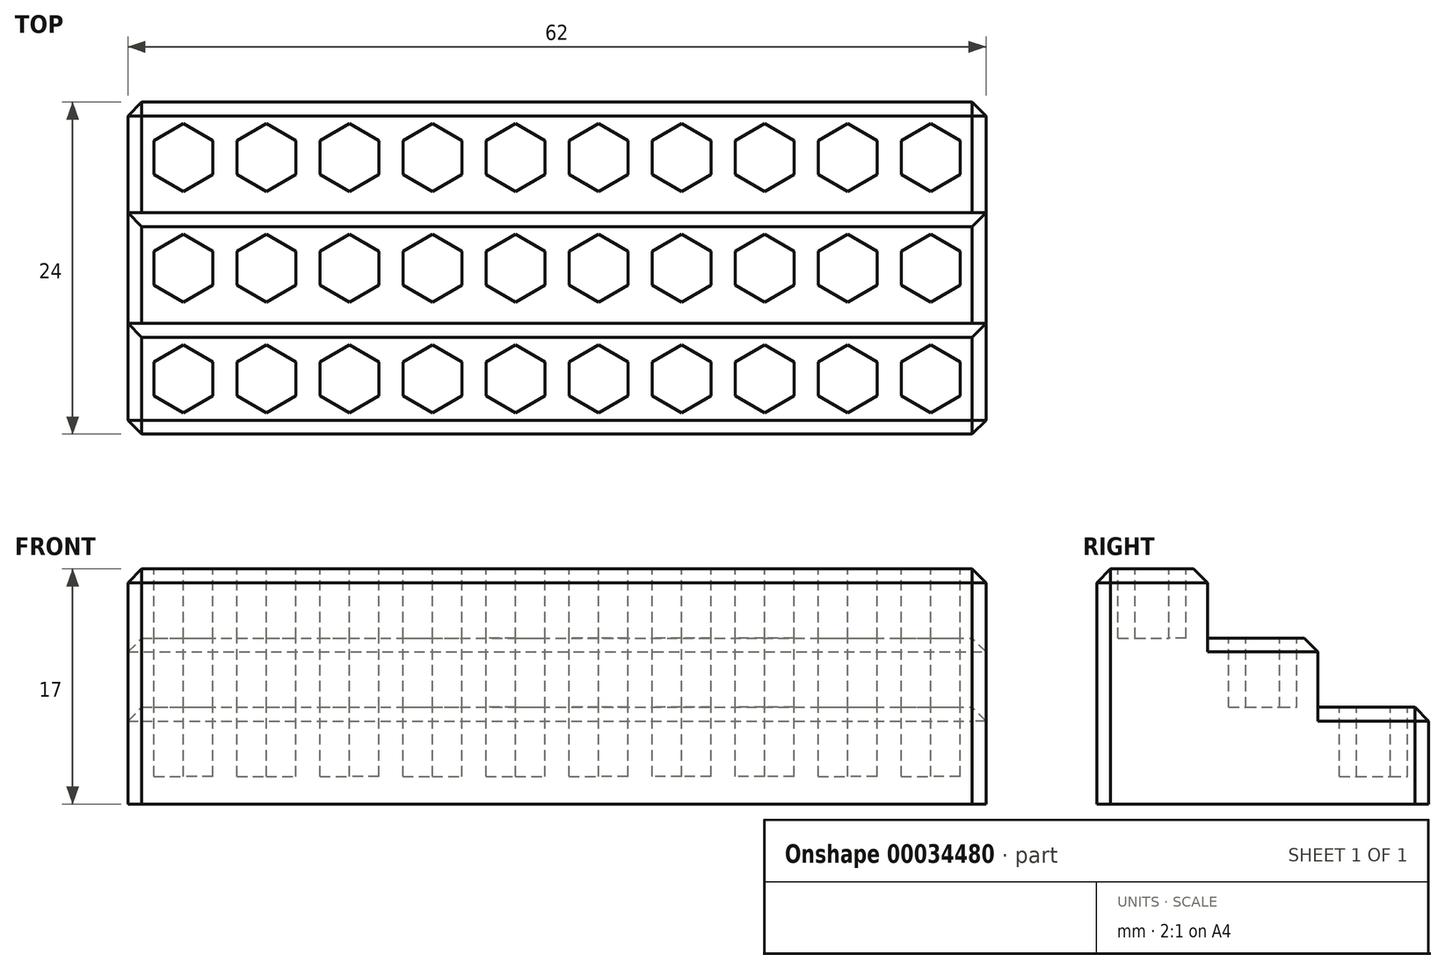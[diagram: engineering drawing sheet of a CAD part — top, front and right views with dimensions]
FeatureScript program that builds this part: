
annotation { "Feature Type Name" : "Feature", "Feature Type Description" : "" }
export const myFeature = defineFeature(function(context is Context, id is Id, definition is map)
    precondition{}
    {
        {
            var Q0;
            Q0=qCreatedBy(makeId("Top.planeOp"),FACE);
            var sketch = newSketch(context, id + "F0", { "sketchPlane" : qUnion([Q0])});
            skLineSegment(sketch, "E0.bottom", {"start": v(0, 0) * mm, "end": v(62, 0) * mm});
            skLineSegment(sketch, "E0.top", {"start": v(0, 8) * mm, "end": v(62, 8) * mm});
            skLineSegment(sketch, "E0.left", {"start": v(0, 0) * mm, "end": v(0, 8) * mm});
            skLineSegment(sketch, "E0.right", {"start": v(62, 0) * mm, "end": v(62, 8) * mm});
            skCircle(sketch, "E1.cCircle", {"center": v(4, 4) * mm, "radius": 2.13 * mm, "construction": true});
            skPoint(sketch, "E1.cCircle.centerSnap0", {"position": v(0, 4) * mm});
            skPoint(sketch, "E1.cCircle.perimeterSnap0", {"position": v(0, 4) * mm});
            skLineSegment(sketch, "E1.0", {"start": v(1.87, 2.77) * mm, "end": v(1.87, 5.23) * mm});
            skLineSegment(sketch, "E1.1", {"start": v(1.87, 5.23) * mm, "end": v(4, 6.45) * mm});
            skLineSegment(sketch, "E1.2", {"start": v(4, 6.45) * mm, "end": v(6.12, 5.23) * mm});
            skLineSegment(sketch, "E1.3", {"start": v(6.12, 5.23) * mm, "end": v(6.12, 2.77) * mm});
            skLineSegment(sketch, "E1.4", {"start": v(6.12, 2.77) * mm, "end": v(4, 1.55) * mm});
            skLineSegment(sketch, "E1.5", {"start": v(4, 1.55) * mm, "end": v(1.87, 2.77) * mm});
            skPoint(sketch, "E1.0.midPoint", {"position": v(1.87, 4) * mm});
            skPoint(sketch, "E1.0.midPoint.positionSnap0", {"position": v(0, 4) * mm});
            skCircle(sketch, "E2.1.0.0", {"center": v(10, 4) * mm, "radius": 2.13 * mm, "construction": true});
            skLineSegment(sketch, "E2.1.0.1", {"start": v(7.87, 5.23) * mm, "end": v(10, 6.45) * mm});
            skLineSegment(sketch, "E2.1.0.2", {"start": v(10, 6.45) * mm, "end": v(12.12, 5.23) * mm});
            skLineSegment(sketch, "E2.1.0.3", {"start": v(12.12, 5.23) * mm, "end": v(12.12, 2.77) * mm});
            skLineSegment(sketch, "E2.1.0.4", {"start": v(12.12, 2.77) * mm, "end": v(10, 1.55) * mm});
            skLineSegment(sketch, "E2.1.0.5", {"start": v(10, 1.55) * mm, "end": v(7.88, 2.77) * mm});
            skPoint(sketch, "E2.1.0.6", {"position": v(7.88, 4) * mm});
            skLineSegment(sketch, "E2.1.0.7", {"start": v(7.88, 2.77) * mm, "end": v(7.88, 5.23) * mm});
            skCircle(sketch, "E2.2.0.0", {"center": v(16, 4) * mm, "radius": 2.13 * mm, "construction": true});
            skLineSegment(sketch, "E2.2.0.1", {"start": v(13.87, 5.23) * mm, "end": v(16, 6.45) * mm});
            skLineSegment(sketch, "E2.2.0.2", {"start": v(16, 6.45) * mm, "end": v(18.13, 5.23) * mm});
            skLineSegment(sketch, "E2.2.0.3", {"start": v(18.12, 5.23) * mm, "end": v(18.12, 2.77) * mm});
            skLineSegment(sketch, "E2.2.0.4", {"start": v(18.13, 2.77) * mm, "end": v(16, 1.55) * mm});
            skLineSegment(sketch, "E2.2.0.5", {"start": v(16, 1.55) * mm, "end": v(13.87, 2.77) * mm});
            skPoint(sketch, "E2.2.0.6", {"position": v(13.87, 4) * mm});
            skLineSegment(sketch, "E2.2.0.7", {"start": v(13.87, 2.77) * mm, "end": v(13.87, 5.23) * mm});
            skCircle(sketch, "E2.3.0.0", {"center": v(22, 4) * mm, "radius": 2.13 * mm, "construction": true});
            skLineSegment(sketch, "E2.3.0.1", {"start": v(19.87, 5.23) * mm, "end": v(22, 6.45) * mm});
            skLineSegment(sketch, "E2.3.0.2", {"start": v(22, 6.45) * mm, "end": v(24.12, 5.23) * mm});
            skLineSegment(sketch, "E2.3.0.3", {"start": v(24.12, 5.23) * mm, "end": v(24.12, 2.77) * mm});
            skLineSegment(sketch, "E2.3.0.4", {"start": v(24.12, 2.77) * mm, "end": v(22, 1.55) * mm});
            skLineSegment(sketch, "E2.3.0.5", {"start": v(22, 1.55) * mm, "end": v(19.88, 2.77) * mm});
            skPoint(sketch, "E2.3.0.6", {"position": v(19.88, 4) * mm});
            skLineSegment(sketch, "E2.3.0.7", {"start": v(19.88, 2.77) * mm, "end": v(19.88, 5.23) * mm});
            skCircle(sketch, "E2.4.0.0", {"center": v(28, 4) * mm, "radius": 2.13 * mm, "construction": true});
            skLineSegment(sketch, "E2.4.0.1", {"start": v(25.87, 5.23) * mm, "end": v(28, 6.45) * mm});
            skLineSegment(sketch, "E2.4.0.2", {"start": v(28, 6.45) * mm, "end": v(30.12, 5.23) * mm});
            skLineSegment(sketch, "E2.4.0.3", {"start": v(30.12, 5.23) * mm, "end": v(30.12, 2.77) * mm});
            skLineSegment(sketch, "E2.4.0.4", {"start": v(30.12, 2.77) * mm, "end": v(28, 1.55) * mm});
            skLineSegment(sketch, "E2.4.0.5", {"start": v(28, 1.55) * mm, "end": v(25.88, 2.77) * mm});
            skPoint(sketch, "E2.4.0.6", {"position": v(25.88, 4) * mm});
            skLineSegment(sketch, "E2.4.0.7", {"start": v(25.88, 2.77) * mm, "end": v(25.88, 5.23) * mm});
            skCircle(sketch, "E2.5.0.0", {"center": v(34, 4) * mm, "radius": 2.13 * mm, "construction": true});
            skLineSegment(sketch, "E2.5.0.1", {"start": v(31.87, 5.23) * mm, "end": v(34, 6.45) * mm});
            skLineSegment(sketch, "E2.5.0.2", {"start": v(34, 6.45) * mm, "end": v(36.12, 5.23) * mm});
            skLineSegment(sketch, "E2.5.0.3", {"start": v(36.12, 5.23) * mm, "end": v(36.12, 2.77) * mm});
            skLineSegment(sketch, "E2.5.0.4", {"start": v(36.12, 2.77) * mm, "end": v(34, 1.55) * mm});
            skLineSegment(sketch, "E2.5.0.5", {"start": v(34, 1.55) * mm, "end": v(31.88, 2.77) * mm});
            skPoint(sketch, "E2.5.0.6", {"position": v(31.88, 4) * mm});
            skLineSegment(sketch, "E2.5.0.7", {"start": v(31.88, 2.77) * mm, "end": v(31.88, 5.23) * mm});
            skCircle(sketch, "E2.6.0.0", {"center": v(40, 4) * mm, "radius": 2.13 * mm, "construction": true});
            skLineSegment(sketch, "E2.6.0.1", {"start": v(37.87, 5.23) * mm, "end": v(40, 6.45) * mm});
            skLineSegment(sketch, "E2.6.0.2", {"start": v(40, 6.45) * mm, "end": v(42.12, 5.23) * mm});
            skLineSegment(sketch, "E2.6.0.3", {"start": v(42.12, 5.23) * mm, "end": v(42.12, 2.77) * mm});
            skLineSegment(sketch, "E2.6.0.4", {"start": v(42.12, 2.77) * mm, "end": v(40, 1.55) * mm});
            skLineSegment(sketch, "E2.6.0.5", {"start": v(40, 1.55) * mm, "end": v(37.88, 2.77) * mm});
            skPoint(sketch, "E2.6.0.6", {"position": v(37.88, 4) * mm});
            skLineSegment(sketch, "E2.6.0.7", {"start": v(37.88, 2.77) * mm, "end": v(37.88, 5.23) * mm});
            skCircle(sketch, "E2.7.0.0", {"center": v(46, 4) * mm, "radius": 2.13 * mm, "construction": true});
            skLineSegment(sketch, "E2.7.0.1", {"start": v(43.87, 5.23) * mm, "end": v(46, 6.45) * mm});
            skLineSegment(sketch, "E2.7.0.2", {"start": v(46, 6.45) * mm, "end": v(48.12, 5.23) * mm});
            skLineSegment(sketch, "E2.7.0.3", {"start": v(48.12, 5.23) * mm, "end": v(48.12, 2.77) * mm});
            skLineSegment(sketch, "E2.7.0.4", {"start": v(48.12, 2.77) * mm, "end": v(46, 1.55) * mm});
            skLineSegment(sketch, "E2.7.0.5", {"start": v(46, 1.55) * mm, "end": v(43.88, 2.77) * mm});
            skPoint(sketch, "E2.7.0.6", {"position": v(43.88, 4) * mm});
            skLineSegment(sketch, "E2.7.0.7", {"start": v(43.88, 2.77) * mm, "end": v(43.88, 5.23) * mm});
            skCircle(sketch, "E2.8.0.0", {"center": v(52, 4) * mm, "radius": 2.13 * mm, "construction": true});
            skLineSegment(sketch, "E2.8.0.1", {"start": v(49.87, 5.23) * mm, "end": v(52, 6.45) * mm});
            skLineSegment(sketch, "E2.8.0.2", {"start": v(52, 6.45) * mm, "end": v(54.12, 5.23) * mm});
            skLineSegment(sketch, "E2.8.0.3", {"start": v(54.12, 5.23) * mm, "end": v(54.12, 2.77) * mm});
            skLineSegment(sketch, "E2.8.0.4", {"start": v(54.12, 2.77) * mm, "end": v(52, 1.55) * mm});
            skLineSegment(sketch, "E2.8.0.5", {"start": v(52, 1.55) * mm, "end": v(49.88, 2.77) * mm});
            skPoint(sketch, "E2.8.0.6", {"position": v(49.88, 4) * mm});
            skLineSegment(sketch, "E2.8.0.7", {"start": v(49.88, 2.77) * mm, "end": v(49.88, 5.23) * mm});
            skCircle(sketch, "E2.9.0.0", {"center": v(58, 4) * mm, "radius": 2.13 * mm, "construction": true});
            skLineSegment(sketch, "E2.9.0.1", {"start": v(55.87, 5.23) * mm, "end": v(58, 6.45) * mm});
            skLineSegment(sketch, "E2.9.0.2", {"start": v(58, 6.45) * mm, "end": v(60.12, 5.23) * mm});
            skLineSegment(sketch, "E2.9.0.3", {"start": v(60.12, 5.23) * mm, "end": v(60.12, 2.77) * mm});
            skLineSegment(sketch, "E2.9.0.4", {"start": v(60.12, 2.77) * mm, "end": v(58, 1.55) * mm});
            skLineSegment(sketch, "E2.9.0.5", {"start": v(58, 1.55) * mm, "end": v(55.88, 2.77) * mm});
            skPoint(sketch, "E2.9.0.6", {"position": v(55.88, 4) * mm});
            skLineSegment(sketch, "E2.9.0.7", {"start": v(55.88, 2.77) * mm, "end": v(55.88, 5.23) * mm});
            skLineSegment(sketch, "E2.direction1", {"start": v(4, 4) * mm, "end": v(10, 4) * mm, "construction": true});
            skPoint(sketch, "E3.0.1.0", {"position": v(13.87, 12) * mm});
            skPoint(sketch, "E3.0.1.1", {"position": v(43.88, 12) * mm});
            skPoint(sketch, "E3.0.1.2", {"position": v(1.87, 12) * mm});
            skPoint(sketch, "E3.0.1.3", {"position": v(25.88, 12) * mm});
            skPoint(sketch, "E3.0.1.4", {"position": v(19.88, 12) * mm});
            skPoint(sketch, "E3.0.1.5", {"position": v(0, 12) * mm});
            skPoint(sketch, "E3.0.1.6", {"position": v(49.88, 12) * mm});
            skLineSegment(sketch, "E3.0.1.8", {"start": v(0, 16) * mm, "end": v(62, 16) * mm});
            skLineSegment(sketch, "E3.0.1.9", {"start": v(62, 8) * mm, "end": v(62, 16) * mm});
            skPoint(sketch, "E3.0.1.10", {"position": v(31.88, 12) * mm});
            skPoint(sketch, "E3.0.1.11", {"position": v(55.88, 12) * mm});
            skPoint(sketch, "E3.0.1.12", {"position": v(7.88, 12) * mm});
            skPoint(sketch, "E3.0.1.13", {"position": v(37.88, 12) * mm});
            skPoint(sketch, "E3.0.1.14", {"position": v(0, 12) * mm});
            skLineSegment(sketch, "E3.0.1.15", {"start": v(30.12, 13.23) * mm, "end": v(30.12, 10.77) * mm});
            skLineSegment(sketch, "E3.0.1.16", {"start": v(40, 9.55) * mm, "end": v(37.88, 10.77) * mm});
            skCircle(sketch, "E3.0.1.17", {"center": v(58, 12) * mm, "radius": 2.13 * mm, "construction": true});
            skLineSegment(sketch, "E3.0.1.18", {"start": v(13.87, 13.23) * mm, "end": v(16, 14.45) * mm});
            skLineSegment(sketch, "E3.0.1.19", {"start": v(4, 12) * mm, "end": v(10, 12) * mm, "construction": true});
            skLineSegment(sketch, "E3.0.1.20", {"start": v(36.12, 13.23) * mm, "end": v(36.12, 10.77) * mm});
            skLineSegment(sketch, "E3.0.1.21", {"start": v(19.87, 13.23) * mm, "end": v(22, 14.45) * mm});
            skLineSegment(sketch, "E3.0.1.22", {"start": v(46, 9.55) * mm, "end": v(43.88, 10.77) * mm});
            skPoint(sketch, "E3.0.1.23", {"position": v(0, 12) * mm});
            skLineSegment(sketch, "E3.0.1.24", {"start": v(43.88, 10.77) * mm, "end": v(43.88, 13.23) * mm});
            skLineSegment(sketch, "E3.0.1.25", {"start": v(36.12, 10.77) * mm, "end": v(34, 9.55) * mm});
            skLineSegment(sketch, "E3.0.1.26", {"start": v(22, 14.45) * mm, "end": v(24.12, 13.23) * mm});
            skLineSegment(sketch, "E3.0.1.27", {"start": v(16, 14.45) * mm, "end": v(18.13, 13.23) * mm});
            skLineSegment(sketch, "E3.0.1.28", {"start": v(49.87, 13.23) * mm, "end": v(52, 14.45) * mm});
            skLineSegment(sketch, "E3.0.1.29", {"start": v(55.87, 13.23) * mm, "end": v(58, 14.45) * mm});
            skLineSegment(sketch, "E3.0.1.30", {"start": v(37.88, 10.77) * mm, "end": v(37.88, 13.23) * mm});
            skLineSegment(sketch, "E3.0.1.31", {"start": v(31.88, 10.77) * mm, "end": v(31.88, 13.23) * mm});
            skLineSegment(sketch, "E3.0.1.32", {"start": v(30.12, 10.77) * mm, "end": v(28, 9.55) * mm});
            skLineSegment(sketch, "E3.0.1.33", {"start": v(24.12, 10.77) * mm, "end": v(22, 9.55) * mm});
            skCircle(sketch, "E3.0.1.34", {"center": v(52, 12) * mm, "radius": 2.13 * mm, "construction": true});
            skLineSegment(sketch, "E3.0.1.35", {"start": v(34, 9.55) * mm, "end": v(31.88, 10.77) * mm});
            skLineSegment(sketch, "E3.0.1.36", {"start": v(24.12, 13.23) * mm, "end": v(24.12, 10.77) * mm});
            skLineSegment(sketch, "E3.0.1.37", {"start": v(18.12, 13.23) * mm, "end": v(18.12, 10.77) * mm});
            skLineSegment(sketch, "E3.0.1.38", {"start": v(58, 14.45) * mm, "end": v(60.12, 13.23) * mm});
            skLineSegment(sketch, "E3.0.1.39", {"start": v(52, 14.45) * mm, "end": v(54.12, 13.23) * mm});
            skCircle(sketch, "E3.0.1.40", {"center": v(46, 12) * mm, "radius": 2.13 * mm, "construction": true});
            skLineSegment(sketch, "E3.0.1.41", {"start": v(28, 9.55) * mm, "end": v(25.88, 10.77) * mm});
            skLineSegment(sketch, "E3.0.1.42", {"start": v(22, 9.55) * mm, "end": v(19.88, 10.77) * mm});
            skLineSegment(sketch, "E3.0.1.43", {"start": v(18.13, 10.77) * mm, "end": v(16, 9.55) * mm});
            skLineSegment(sketch, "E3.0.1.44", {"start": v(54.12, 13.23) * mm, "end": v(54.12, 10.77) * mm});
            skLineSegment(sketch, "E3.0.1.45", {"start": v(60.12, 13.23) * mm, "end": v(60.12, 10.77) * mm});
            skLineSegment(sketch, "E3.0.1.46", {"start": v(43.87, 13.23) * mm, "end": v(46, 14.45) * mm});
            skLineSegment(sketch, "E3.0.1.47", {"start": v(37.87, 13.23) * mm, "end": v(40, 14.45) * mm});
            skLineSegment(sketch, "E3.0.1.48", {"start": v(25.88, 10.77) * mm, "end": v(25.88, 13.23) * mm});
            skLineSegment(sketch, "E3.0.1.49", {"start": v(10, 14.45) * mm, "end": v(12.12, 13.23) * mm});
            skLineSegment(sketch, "E3.0.1.50", {"start": v(19.88, 10.77) * mm, "end": v(19.88, 13.23) * mm});
            skLineSegment(sketch, "E3.0.1.51", {"start": v(12.12, 13.23) * mm, "end": v(12.12, 10.77) * mm});
            skLineSegment(sketch, "E3.0.1.52", {"start": v(12.12, 10.77) * mm, "end": v(10, 9.55) * mm});
            skLineSegment(sketch, "E3.0.1.53", {"start": v(0, 8) * mm, "end": v(0, 16) * mm});
            skCircle(sketch, "E3.0.1.54", {"center": v(4, 12) * mm, "radius": 2.13 * mm, "construction": true});
            skLineSegment(sketch, "E3.0.1.55", {"start": v(1.87, 13.23) * mm, "end": v(4, 14.45) * mm});
            skLineSegment(sketch, "E3.0.1.56", {"start": v(4, 14.45) * mm, "end": v(6.12, 13.23) * mm});
            skLineSegment(sketch, "E3.0.1.57", {"start": v(6.12, 13.23) * mm, "end": v(6.12, 10.77) * mm});
            skLineSegment(sketch, "E3.0.1.58", {"start": v(6.12, 10.77) * mm, "end": v(4, 9.55) * mm});
            skLineSegment(sketch, "E3.0.1.59", {"start": v(4, 9.55) * mm, "end": v(1.87, 10.77) * mm});
            skCircle(sketch, "E3.0.1.60", {"center": v(10, 12) * mm, "radius": 2.13 * mm, "construction": true});
            skLineSegment(sketch, "E3.0.1.61", {"start": v(7.87, 13.23) * mm, "end": v(10, 14.45) * mm});
            skLineSegment(sketch, "E3.0.1.62", {"start": v(46, 14.45) * mm, "end": v(48.12, 13.23) * mm});
            skLineSegment(sketch, "E3.0.1.63", {"start": v(16, 9.55) * mm, "end": v(13.87, 10.77) * mm});
            skCircle(sketch, "E3.0.1.64", {"center": v(34, 12) * mm, "radius": 2.13 * mm, "construction": true});
            skLineSegment(sketch, "E3.0.1.65", {"start": v(60.12, 10.77) * mm, "end": v(58, 9.55) * mm});
            skLineSegment(sketch, "E3.0.1.66", {"start": v(10, 9.55) * mm, "end": v(7.88, 10.77) * mm});
            skLineSegment(sketch, "E3.0.1.67", {"start": v(54.12, 10.77) * mm, "end": v(52, 9.55) * mm});
            skLineSegment(sketch, "E3.0.1.68", {"start": v(40, 14.45) * mm, "end": v(42.12, 13.23) * mm});
            skLineSegment(sketch, "E3.0.1.69", {"start": v(48.12, 13.23) * mm, "end": v(48.12, 10.77) * mm});
            skLineSegment(sketch, "E3.0.1.70", {"start": v(13.87, 10.77) * mm, "end": v(13.87, 13.23) * mm});
            skLineSegment(sketch, "E3.0.1.71", {"start": v(31.87, 13.23) * mm, "end": v(34, 14.45) * mm});
            skLineSegment(sketch, "E3.0.1.72", {"start": v(58, 9.55) * mm, "end": v(55.88, 10.77) * mm});
            skLineSegment(sketch, "E3.0.1.73", {"start": v(7.88, 10.77) * mm, "end": v(7.88, 13.23) * mm});
            skLineSegment(sketch, "E3.0.1.74", {"start": v(52, 9.55) * mm, "end": v(49.88, 10.77) * mm});
            skLineSegment(sketch, "E3.0.1.75", {"start": v(25.87, 13.23) * mm, "end": v(28, 14.45) * mm});
            skLineSegment(sketch, "E3.0.1.76", {"start": v(42.12, 13.23) * mm, "end": v(42.12, 10.77) * mm});
            skLineSegment(sketch, "E3.0.1.77", {"start": v(48.12, 10.77) * mm, "end": v(46, 9.55) * mm});
            skCircle(sketch, "E3.0.1.78", {"center": v(22, 12) * mm, "radius": 2.13 * mm, "construction": true});
            skLineSegment(sketch, "E3.0.1.79", {"start": v(34, 14.45) * mm, "end": v(36.12, 13.23) * mm});
            skLineSegment(sketch, "E3.0.1.80", {"start": v(55.88, 10.77) * mm, "end": v(55.88, 13.23) * mm});
            skCircle(sketch, "E3.0.1.81", {"center": v(16, 12) * mm, "radius": 2.13 * mm, "construction": true});
            skLineSegment(sketch, "E3.0.1.82", {"start": v(49.88, 10.77) * mm, "end": v(49.88, 13.23) * mm});
            skLineSegment(sketch, "E3.0.1.83", {"start": v(42.12, 10.77) * mm, "end": v(40, 9.55) * mm});
            skLineSegment(sketch, "E3.0.1.84", {"start": v(28, 14.45) * mm, "end": v(30.12, 13.23) * mm});
            skCircle(sketch, "E3.0.1.85", {"center": v(40, 12) * mm, "radius": 2.13 * mm, "construction": true});
            skLineSegment(sketch, "E3.0.1.86", {"start": v(1.87, 10.77) * mm, "end": v(1.87, 13.23) * mm});
            skCircle(sketch, "E3.0.1.87", {"center": v(28, 12) * mm, "radius": 2.13 * mm, "construction": true});
            skPoint(sketch, "E3.0.2.0", {"position": v(13.87, 20) * mm});
            skPoint(sketch, "E3.0.2.1", {"position": v(43.88, 20) * mm});
            skPoint(sketch, "E3.0.2.2", {"position": v(1.87, 20) * mm});
            skPoint(sketch, "E3.0.2.3", {"position": v(25.88, 20) * mm});
            skPoint(sketch, "E3.0.2.4", {"position": v(19.88, 20) * mm});
            skPoint(sketch, "E3.0.2.5", {"position": v(0, 20) * mm});
            skPoint(sketch, "E3.0.2.6", {"position": v(49.88, 20) * mm});
            skLineSegment(sketch, "E3.0.2.7", {"start": v(0, 16) * mm, "end": v(62, 16) * mm});
            skLineSegment(sketch, "E3.0.2.8", {"start": v(0, 24) * mm, "end": v(62, 24) * mm});
            skLineSegment(sketch, "E3.0.2.9", {"start": v(62, 16) * mm, "end": v(62, 24) * mm});
            skPoint(sketch, "E3.0.2.10", {"position": v(31.88, 20) * mm});
            skPoint(sketch, "E3.0.2.11", {"position": v(55.88, 20) * mm});
            skPoint(sketch, "E3.0.2.12", {"position": v(7.88, 20) * mm});
            skPoint(sketch, "E3.0.2.13", {"position": v(37.88, 20) * mm});
            skPoint(sketch, "E3.0.2.14", {"position": v(0, 20) * mm});
            skLineSegment(sketch, "E3.0.2.15", {"start": v(30.12, 21.23) * mm, "end": v(30.12, 18.77) * mm});
            skLineSegment(sketch, "E3.0.2.16", {"start": v(40, 17.55) * mm, "end": v(37.88, 18.77) * mm});
            skCircle(sketch, "E3.0.2.17", {"center": v(58, 20) * mm, "radius": 2.13 * mm, "construction": true});
            skLineSegment(sketch, "E3.0.2.18", {"start": v(13.87, 21.23) * mm, "end": v(16, 22.45) * mm});
            skLineSegment(sketch, "E3.0.2.19", {"start": v(4, 20) * mm, "end": v(10, 20) * mm, "construction": true});
            skLineSegment(sketch, "E3.0.2.20", {"start": v(36.12, 21.23) * mm, "end": v(36.12, 18.77) * mm});
            skLineSegment(sketch, "E3.0.2.21", {"start": v(19.87, 21.23) * mm, "end": v(22, 22.45) * mm});
            skLineSegment(sketch, "E3.0.2.22", {"start": v(46, 17.55) * mm, "end": v(43.88, 18.77) * mm});
            skPoint(sketch, "E3.0.2.23", {"position": v(0, 20) * mm});
            skLineSegment(sketch, "E3.0.2.24", {"start": v(43.88, 18.77) * mm, "end": v(43.88, 21.23) * mm});
            skLineSegment(sketch, "E3.0.2.25", {"start": v(36.12, 18.77) * mm, "end": v(34, 17.55) * mm});
            skLineSegment(sketch, "E3.0.2.26", {"start": v(22, 22.45) * mm, "end": v(24.12, 21.23) * mm});
            skLineSegment(sketch, "E3.0.2.27", {"start": v(16, 22.45) * mm, "end": v(18.13, 21.23) * mm});
            skLineSegment(sketch, "E3.0.2.28", {"start": v(49.87, 21.23) * mm, "end": v(52, 22.45) * mm});
            skLineSegment(sketch, "E3.0.2.29", {"start": v(55.87, 21.23) * mm, "end": v(58, 22.45) * mm});
            skLineSegment(sketch, "E3.0.2.30", {"start": v(37.88, 18.77) * mm, "end": v(37.88, 21.23) * mm});
            skLineSegment(sketch, "E3.0.2.31", {"start": v(31.88, 18.77) * mm, "end": v(31.88, 21.23) * mm});
            skLineSegment(sketch, "E3.0.2.32", {"start": v(30.12, 18.77) * mm, "end": v(28, 17.55) * mm});
            skLineSegment(sketch, "E3.0.2.33", {"start": v(24.12, 18.77) * mm, "end": v(22, 17.55) * mm});
            skCircle(sketch, "E3.0.2.34", {"center": v(52, 20) * mm, "radius": 2.13 * mm, "construction": true});
            skLineSegment(sketch, "E3.0.2.35", {"start": v(34, 17.55) * mm, "end": v(31.88, 18.77) * mm});
            skLineSegment(sketch, "E3.0.2.36", {"start": v(24.12, 21.23) * mm, "end": v(24.12, 18.77) * mm});
            skLineSegment(sketch, "E3.0.2.37", {"start": v(18.12, 21.23) * mm, "end": v(18.12, 18.77) * mm});
            skLineSegment(sketch, "E3.0.2.38", {"start": v(58, 22.45) * mm, "end": v(60.12, 21.23) * mm});
            skLineSegment(sketch, "E3.0.2.39", {"start": v(52, 22.45) * mm, "end": v(54.12, 21.23) * mm});
            skCircle(sketch, "E3.0.2.40", {"center": v(46, 20) * mm, "radius": 2.13 * mm, "construction": true});
            skLineSegment(sketch, "E3.0.2.41", {"start": v(28, 17.55) * mm, "end": v(25.88, 18.77) * mm});
            skLineSegment(sketch, "E3.0.2.42", {"start": v(22, 17.55) * mm, "end": v(19.88, 18.77) * mm});
            skLineSegment(sketch, "E3.0.2.43", {"start": v(18.13, 18.77) * mm, "end": v(16, 17.55) * mm});
            skLineSegment(sketch, "E3.0.2.44", {"start": v(54.12, 21.23) * mm, "end": v(54.12, 18.77) * mm});
            skLineSegment(sketch, "E3.0.2.45", {"start": v(60.12, 21.23) * mm, "end": v(60.12, 18.77) * mm});
            skLineSegment(sketch, "E3.0.2.46", {"start": v(43.87, 21.23) * mm, "end": v(46, 22.45) * mm});
            skLineSegment(sketch, "E3.0.2.47", {"start": v(37.87, 21.23) * mm, "end": v(40, 22.45) * mm});
            skLineSegment(sketch, "E3.0.2.48", {"start": v(25.88, 18.77) * mm, "end": v(25.88, 21.23) * mm});
            skLineSegment(sketch, "E3.0.2.49", {"start": v(10, 22.45) * mm, "end": v(12.12, 21.23) * mm});
            skLineSegment(sketch, "E3.0.2.50", {"start": v(19.88, 18.77) * mm, "end": v(19.88, 21.23) * mm});
            skLineSegment(sketch, "E3.0.2.51", {"start": v(12.12, 21.23) * mm, "end": v(12.12, 18.77) * mm});
            skLineSegment(sketch, "E3.0.2.52", {"start": v(12.12, 18.77) * mm, "end": v(10, 17.55) * mm});
            skLineSegment(sketch, "E3.0.2.53", {"start": v(0, 16) * mm, "end": v(0, 24) * mm});
            skCircle(sketch, "E3.0.2.54", {"center": v(4, 20) * mm, "radius": 2.13 * mm, "construction": true});
            skLineSegment(sketch, "E3.0.2.55", {"start": v(1.87, 21.23) * mm, "end": v(4, 22.45) * mm});
            skLineSegment(sketch, "E3.0.2.56", {"start": v(4, 22.45) * mm, "end": v(6.12, 21.23) * mm});
            skLineSegment(sketch, "E3.0.2.57", {"start": v(6.12, 21.23) * mm, "end": v(6.12, 18.77) * mm});
            skLineSegment(sketch, "E3.0.2.58", {"start": v(6.13, 18.77) * mm, "end": v(4, 17.55) * mm});
            skLineSegment(sketch, "E3.0.2.59", {"start": v(4, 17.55) * mm, "end": v(1.87, 18.77) * mm});
            skCircle(sketch, "E3.0.2.60", {"center": v(10, 20) * mm, "radius": 2.13 * mm, "construction": true});
            skLineSegment(sketch, "E3.0.2.61", {"start": v(7.87, 21.23) * mm, "end": v(10, 22.45) * mm});
            skLineSegment(sketch, "E3.0.2.62", {"start": v(46, 22.45) * mm, "end": v(48.12, 21.23) * mm});
            skLineSegment(sketch, "E3.0.2.63", {"start": v(16, 17.55) * mm, "end": v(13.87, 18.77) * mm});
            skCircle(sketch, "E3.0.2.64", {"center": v(34, 20) * mm, "radius": 2.13 * mm, "construction": true});
            skLineSegment(sketch, "E3.0.2.65", {"start": v(60.12, 18.77) * mm, "end": v(58, 17.55) * mm});
            skLineSegment(sketch, "E3.0.2.66", {"start": v(10, 17.55) * mm, "end": v(7.88, 18.77) * mm});
            skLineSegment(sketch, "E3.0.2.67", {"start": v(54.12, 18.77) * mm, "end": v(52, 17.55) * mm});
            skLineSegment(sketch, "E3.0.2.68", {"start": v(40, 22.45) * mm, "end": v(42.12, 21.23) * mm});
            skLineSegment(sketch, "E3.0.2.69", {"start": v(48.12, 21.23) * mm, "end": v(48.12, 18.77) * mm});
            skLineSegment(sketch, "E3.0.2.70", {"start": v(13.87, 18.77) * mm, "end": v(13.87, 21.23) * mm});
            skLineSegment(sketch, "E3.0.2.71", {"start": v(31.87, 21.23) * mm, "end": v(34, 22.45) * mm});
            skLineSegment(sketch, "E3.0.2.72", {"start": v(58, 17.55) * mm, "end": v(55.88, 18.77) * mm});
            skLineSegment(sketch, "E3.0.2.73", {"start": v(7.88, 18.77) * mm, "end": v(7.88, 21.23) * mm});
            skLineSegment(sketch, "E3.0.2.74", {"start": v(52, 17.55) * mm, "end": v(49.88, 18.77) * mm});
            skLineSegment(sketch, "E3.0.2.75", {"start": v(25.87, 21.23) * mm, "end": v(28, 22.45) * mm});
            skLineSegment(sketch, "E3.0.2.76", {"start": v(42.12, 21.23) * mm, "end": v(42.12, 18.77) * mm});
            skLineSegment(sketch, "E3.0.2.77", {"start": v(48.12, 18.77) * mm, "end": v(46, 17.55) * mm});
            skCircle(sketch, "E3.0.2.78", {"center": v(22, 20) * mm, "radius": 2.13 * mm, "construction": true});
            skLineSegment(sketch, "E3.0.2.79", {"start": v(34, 22.45) * mm, "end": v(36.12, 21.23) * mm});
            skLineSegment(sketch, "E3.0.2.80", {"start": v(55.88, 18.77) * mm, "end": v(55.88, 21.23) * mm});
            skCircle(sketch, "E3.0.2.81", {"center": v(16, 20) * mm, "radius": 2.13 * mm, "construction": true});
            skLineSegment(sketch, "E3.0.2.82", {"start": v(49.88, 18.77) * mm, "end": v(49.88, 21.23) * mm});
            skLineSegment(sketch, "E3.0.2.83", {"start": v(42.12, 18.77) * mm, "end": v(40, 17.55) * mm});
            skLineSegment(sketch, "E3.0.2.84", {"start": v(28, 22.45) * mm, "end": v(30.12, 21.23) * mm});
            skCircle(sketch, "E3.0.2.85", {"center": v(40, 20) * mm, "radius": 2.13 * mm, "construction": true});
            skLineSegment(sketch, "E3.0.2.86", {"start": v(1.87, 18.77) * mm, "end": v(1.87, 21.23) * mm});
            skCircle(sketch, "E3.0.2.87", {"center": v(28, 20) * mm, "radius": 2.13 * mm, "construction": true});
            skLineSegment(sketch, "E3.direction1", {"start": v(13.87, 4) * mm, "end": v(38.88, 4) * mm, "construction": true});
            skLineSegment(sketch, "E3.direction2", {"start": v(13.87, 4) * mm, "end": v(13.87, 12) * mm, "construction": true});
            skSolve(sketch);
        }
        {
            var Q0;
            Q0=qCreatedBy(makeId("Top.planeOp"),FACE);
            cPlane(context, id + "F1", {"entities" : qUnion([Q0]), "cplaneType" : CPlaneType.OFFSET, "offset" : 20 * mm, "oppositeDirection" : true, "width" : 150 * mm, "height" : 150 * mm});
        }
        {
            var Q0;
            Q0=qCreatedBy(id+"F1.planeOp",FACE);
            var sketch = newSketch(context, id + "F2", { "sketchPlane" : qUnion([Q0])});
            skLineSegment(sketch, "E4.0", {"start": v(0, 8) * mm, "end": v(62, 8) * mm});
            skLineSegment(sketch, "E5.0", {"start": v(62, 0) * mm, "end": v(62, 8) * mm});
            skLineSegment(sketch, "E6.0", {"start": v(0, 0) * mm, "end": v(62, 0) * mm});
            skLineSegment(sketch, "E7.0", {"start": v(0, 0) * mm, "end": v(0, 8) * mm});
            skLineSegment(sketch, "E8.0", {"start": v(0, 8) * mm, "end": v(0, 16) * mm});
            skLineSegment(sketch, "E9.0", {"start": v(0, 16) * mm, "end": v(62, 16) * mm});
            skLineSegment(sketch, "E10.0", {"start": v(62, 8) * mm, "end": v(62, 16) * mm});
            skLineSegment(sketch, "E11.0", {"start": v(62, 16) * mm, "end": v(62, 24) * mm});
            skLineSegment(sketch, "E11.1", {"start": v(0, 24) * mm, "end": v(62, 24) * mm});
            skLineSegment(sketch, "E11.2", {"start": v(0, 16) * mm, "end": v(0, 24) * mm});
            skSolve(sketch);
        }
        {
            var Q0;
            Q0=makeQuery(id+"F2.imprint","IMPRINT",FACE,{"disambiguationData":[TD([[makeQuery(id+"F2.imprint","IMPRINT",EDGE,{"derivedFrom":sQuery(id+"F2.wireOp",EDGE,"E4.0")}),-1.0]])]});
            extrude(context, id + "F3", {"entities" : qUnion([Q0]), "depth" : 17 * mm});
        }
        {
            var Q0;
            Q0=makeQuery(id+"F2.imprint","IMPRINT",FACE,{"disambiguationData":[TD([[makeQuery(id+"F2.imprint","IMPRINT",EDGE,{"derivedFrom":sQuery(id+"F2.wireOp",EDGE,"E4.0")}),1.0]])]});
            extrude(context, id + "F4", {"entities" : qUnion([Q0]), "operationType" : NewBodyOperationType.ADD, "depth" : 12 * mm});
        }
        {
            var Q0;
            Q0=makeQuery(id+"F2.imprint","IMPRINT",FACE,{"disambiguationData":[TD([[makeQuery(id+"F2.imprint","IMPRINT",EDGE,{"derivedFrom":sQuery(id+"F2.wireOp",EDGE,"E9.0")}),1.0]])]});
            extrude(context, id + "F5", {"entities" : qUnion([Q0]), "operationType" : NewBodyOperationType.ADD, "depth" : 7 * mm});
        }
        {
            var Q0;
            Q0=makeQuery(id+"F0.imprint","IMPRINT",FACE,{"disambiguationData":[TD([[makeQuery(id+"F0.imprint","IMPRINT",EDGE,{"derivedFrom":sQuery(id+"F0.wireOp",EDGE,"E2.9.0.1")}),-1.0]])]});
            var Q1;
            Q1=makeQuery(id+"F0.imprint","IMPRINT",FACE,{"disambiguationData":[TD([[makeQuery(id+"F0.imprint","IMPRINT",EDGE,{"derivedFrom":sQuery(id+"F0.wireOp",EDGE,"E2.8.0.1")}),-1.0]])]});
            var Q2;
            Q2=makeQuery(id+"F0.imprint","IMPRINT",FACE,{"disambiguationData":[TD([[makeQuery(id+"F0.imprint","IMPRINT",EDGE,{"derivedFrom":sQuery(id+"F0.wireOp",EDGE,"E2.7.0.1")}),-1.0]])]});
            var Q3;
            Q3=makeQuery(id+"F0.imprint","IMPRINT",FACE,{"disambiguationData":[TD([[makeQuery(id+"F0.imprint","IMPRINT",EDGE,{"derivedFrom":sQuery(id+"F0.wireOp",EDGE,"E2.6.0.1")}),-1.0]])]});
            var Q4;
            Q4=makeQuery(id+"F0.imprint","IMPRINT",FACE,{"disambiguationData":[TD([[makeQuery(id+"F0.imprint","IMPRINT",EDGE,{"derivedFrom":sQuery(id+"F0.wireOp",EDGE,"E2.5.0.1")}),-1.0]])]});
            var Q5;
            Q5=makeQuery(id+"F0.imprint","IMPRINT",FACE,{"disambiguationData":[TD([[makeQuery(id+"F0.imprint","IMPRINT",EDGE,{"derivedFrom":sQuery(id+"F0.wireOp",EDGE,"E2.4.0.1")}),-1.0]])]});
            var Q6;
            Q6=makeQuery(id+"F0.imprint","IMPRINT",FACE,{"disambiguationData":[TD([[makeQuery(id+"F0.imprint","IMPRINT",EDGE,{"derivedFrom":sQuery(id+"F0.wireOp",EDGE,"E2.3.0.1")}),-1.0]])]});
            var Q7;
            Q7=makeQuery(id+"F0.imprint","IMPRINT",FACE,{"disambiguationData":[TD([[makeQuery(id+"F0.imprint","IMPRINT",EDGE,{"derivedFrom":sQuery(id+"F0.wireOp",EDGE,"E2.2.0.1")}),-1.0]])]});
            var Q8;
            Q8=makeQuery(id+"F0.imprint","IMPRINT",FACE,{"disambiguationData":[TD([[makeQuery(id+"F0.imprint","IMPRINT",EDGE,{"derivedFrom":sQuery(id+"F0.wireOp",EDGE,"E2.1.0.1")}),-1.0]])]});
            var Q9;
            Q9=makeQuery(id+"F0.imprint","IMPRINT",FACE,{"disambiguationData":[TD([[makeQuery(id+"F0.imprint","IMPRINT",EDGE,{"derivedFrom":sQuery(id+"F0.wireOp",EDGE,"E1.0")}),-1.0]])]});
            extrude(context, id + "F6", {"entities" : qUnion([Q0, Q1, Q2, Q3, Q4, Q5, Q6, Q7, Q8, Q9]), "operationType" : NewBodyOperationType.REMOVE, "oppositeDirection" : true, "depth" : 8 * mm});
        }
        {
            var Q0;
            Q0=makeQuery(id+"F0.imprint","IMPRINT",FACE,{"disambiguationData":[TD([[makeQuery(id+"F0.imprint","IMPRINT",EDGE,{"derivedFrom":sQuery(id+"F0.wireOp",EDGE,"E3.0.1.29")}),-1.0]])]});
            var Q1;
            Q1=makeQuery(id+"F0.imprint","IMPRINT",FACE,{"disambiguationData":[TD([[makeQuery(id+"F0.imprint","IMPRINT",EDGE,{"derivedFrom":sQuery(id+"F0.wireOp",EDGE,"E3.0.1.28")}),-1.0]])]});
            var Q2;
            Q2=makeQuery(id+"F0.imprint","IMPRINT",FACE,{"disambiguationData":[TD([[makeQuery(id+"F0.imprint","IMPRINT",EDGE,{"derivedFrom":sQuery(id+"F0.wireOp",EDGE,"E3.0.1.22")}),-1.0]])]});
            var Q3;
            Q3=makeQuery(id+"F0.imprint","IMPRINT",FACE,{"disambiguationData":[TD([[makeQuery(id+"F0.imprint","IMPRINT",EDGE,{"derivedFrom":sQuery(id+"F0.wireOp",EDGE,"E3.0.1.16")}),-1.0]])]});
            var Q4;
            Q4=makeQuery(id+"F0.imprint","IMPRINT",FACE,{"disambiguationData":[TD([[makeQuery(id+"F0.imprint","IMPRINT",EDGE,{"derivedFrom":sQuery(id+"F0.wireOp",EDGE,"E3.0.1.20")}),-1.0]])]});
            var Q5;
            Q5=makeQuery(id+"F0.imprint","IMPRINT",FACE,{"disambiguationData":[TD([[makeQuery(id+"F0.imprint","IMPRINT",EDGE,{"derivedFrom":sQuery(id+"F0.wireOp",EDGE,"E3.0.1.15")}),-1.0]])]});
            var Q6;
            Q6=makeQuery(id+"F0.imprint","IMPRINT",FACE,{"disambiguationData":[TD([[makeQuery(id+"F0.imprint","IMPRINT",EDGE,{"derivedFrom":sQuery(id+"F0.wireOp",EDGE,"E3.0.1.21")}),-1.0]])]});
            var Q7;
            Q7=makeQuery(id+"F0.imprint","IMPRINT",FACE,{"disambiguationData":[TD([[makeQuery(id+"F0.imprint","IMPRINT",EDGE,{"derivedFrom":sQuery(id+"F0.wireOp",EDGE,"E3.0.1.18")}),-1.0]])]});
            var Q8;
            Q8=makeQuery(id+"F0.imprint","IMPRINT",FACE,{"disambiguationData":[TD([[makeQuery(id+"F0.imprint","IMPRINT",EDGE,{"derivedFrom":sQuery(id+"F0.wireOp",EDGE,"E3.0.1.49")}),-1.0]])]});
            var Q9;
            Q9=makeQuery(id+"F0.imprint","IMPRINT",FACE,{"disambiguationData":[TD([[makeQuery(id+"F0.imprint","IMPRINT",EDGE,{"derivedFrom":sQuery(id+"F0.wireOp",EDGE,"E3.0.1.55")}),-1.0]])]});
            extrude(context, id + "F7", {"entities" : qUnion([Q0, Q1, Q2, Q3, Q4, Q5, Q6, Q7, Q8, Q9]), "operationType" : NewBodyOperationType.REMOVE, "oppositeDirection" : true, "depth" : 13 * mm});
        }
        {
            var Q0;
            Q0=makeQuery(id+"F0.imprint","IMPRINT",FACE,{"disambiguationData":[TD([[makeQuery(id+"F0.imprint","IMPRINT",EDGE,{"derivedFrom":sQuery(id+"F0.wireOp",EDGE,"E3.0.2.29")}),-1.0]])]});
            var Q1;
            Q1=makeQuery(id+"F0.imprint","IMPRINT",FACE,{"disambiguationData":[TD([[makeQuery(id+"F0.imprint","IMPRINT",EDGE,{"derivedFrom":sQuery(id+"F0.wireOp",EDGE,"E3.0.2.28")}),-1.0]])]});
            var Q2;
            Q2=makeQuery(id+"F0.imprint","IMPRINT",FACE,{"disambiguationData":[TD([[makeQuery(id+"F0.imprint","IMPRINT",EDGE,{"derivedFrom":sQuery(id+"F0.wireOp",EDGE,"E3.0.2.22")}),-1.0]])]});
            var Q3;
            Q3=makeQuery(id+"F0.imprint","IMPRINT",FACE,{"disambiguationData":[TD([[makeQuery(id+"F0.imprint","IMPRINT",EDGE,{"derivedFrom":sQuery(id+"F0.wireOp",EDGE,"E3.0.2.16")}),-1.0]])]});
            var Q4;
            Q4=makeQuery(id+"F0.imprint","IMPRINT",FACE,{"disambiguationData":[TD([[makeQuery(id+"F0.imprint","IMPRINT",EDGE,{"derivedFrom":sQuery(id+"F0.wireOp",EDGE,"E3.0.2.20")}),-1.0]])]});
            var Q5;
            Q5=makeQuery(id+"F0.imprint","IMPRINT",FACE,{"disambiguationData":[TD([[makeQuery(id+"F0.imprint","IMPRINT",EDGE,{"derivedFrom":sQuery(id+"F0.wireOp",EDGE,"E3.0.2.15")}),-1.0]])]});
            var Q6;
            Q6=makeQuery(id+"F0.imprint","IMPRINT",FACE,{"disambiguationData":[TD([[makeQuery(id+"F0.imprint","IMPRINT",EDGE,{"derivedFrom":sQuery(id+"F0.wireOp",EDGE,"E3.0.2.21")}),-1.0]])]});
            var Q7;
            Q7=makeQuery(id+"F0.imprint","IMPRINT",FACE,{"disambiguationData":[TD([[makeQuery(id+"F0.imprint","IMPRINT",EDGE,{"derivedFrom":sQuery(id+"F0.wireOp",EDGE,"E3.0.2.18")}),-1.0]])]});
            var Q8;
            Q8=makeQuery(id+"F0.imprint","IMPRINT",FACE,{"disambiguationData":[TD([[makeQuery(id+"F0.imprint","IMPRINT",EDGE,{"derivedFrom":sQuery(id+"F0.wireOp",EDGE,"E3.0.2.49")}),-1.0]])]});
            var Q9;
            Q9=makeQuery(id+"F0.imprint","IMPRINT",FACE,{"disambiguationData":[TD([[makeQuery(id+"F0.imprint","IMPRINT",EDGE,{"derivedFrom":sQuery(id+"F0.wireOp",EDGE,"E3.0.2.55")}),-1.0]])]});
            extrude(context, id + "F8", {"entities" : qUnion([Q0, Q1, Q2, Q3, Q4, Q5, Q6, Q7, Q8, Q9]), "operationType" : NewBodyOperationType.REMOVE, "oppositeDirection" : true, "depth" : 18 * mm});
        }
        {
            var Q0;
            Q0=makeQuery(id+"F3.opExtrude","CAP_EDGE",EDGE,{"disambiguationData":[OSD([sQuery(id+"F2.wireOp",EDGE,"E4.0")])],"isStart":false});
            var Q1;
            Q1=makeQuery(id+"F4.opExtrude","CAP_EDGE",EDGE,{"disambiguationData":[OSD([sQuery(id+"F2.wireOp",EDGE,"E9.0")])],"isStart":false});
            var Q2;
            Q2=makeQuery(id+"F5.opExtrude","CAP_EDGE",EDGE,{"disambiguationData":[OSD([sQuery(id+"F2.wireOp",EDGE,"E11.1")])],"isStart":false});
            var Q3;
            Q3=makeQuery(id+"F5.opExtrude","CAP_EDGE",EDGE,{"disambiguationData":[OSD([sQuery(id+"F2.wireOp",EDGE,"E9.0")])],"isStart":false});
            var Q4;
            Q4=makeQuery(id+"F4.opExtrude","CAP_EDGE",EDGE,{"disambiguationData":[OSD([sQuery(id+"F2.wireOp",EDGE,"E4.0")])],"isStart":false});
            var Q5;
            Q5=makeQuery(id+"F3.opExtrude","CAP_EDGE",EDGE,{"disambiguationData":[OSD([sQuery(id+"F2.wireOp",EDGE,"E5.0")])],"isStart":false});
            var Q6;
            Q6=makeQuery(id+"F4.opExtrude","CAP_EDGE",EDGE,{"disambiguationData":[OSD([sQuery(id+"F2.wireOp",EDGE,"E10.0")])],"isStart":false});
            var Q7;
            Q7=makeQuery(id+"F5.opExtrude","CAP_EDGE",EDGE,{"disambiguationData":[OSD([sQuery(id+"F2.wireOp",EDGE,"E11.0")])],"isStart":false});
            var Q8;
            Q8=makeQuery(id+"F3.opExtrude","CAP_EDGE",EDGE,{"disambiguationData":[OSD([sQuery(id+"F2.wireOp",EDGE,"E6.0")])],"isStart":false});
            var Q9;
            Q9=makeQuery(id+"F3.opExtrude","SWEPT_EDGE",EDGE,{"disambiguationData":[OSD([sQuery(id+"F2.wireOp",EDGE,"E5.0"),sQuery(id+"F2.wireOp",EDGE,"E6.0")])]});
            var Q10;
            Q10=makeQuery(id+"F5.opExtrude","SWEPT_EDGE",EDGE,{"disambiguationData":[OSD([sQuery(id+"F2.wireOp",EDGE,"E11.0"),sQuery(id+"F2.wireOp",EDGE,"E11.1")])]});
            var Q11;
            Q11=makeQuery(id+"F5.opExtrude","SWEPT_EDGE",EDGE,{"disambiguationData":[OSD([sQuery(id+"F2.wireOp",EDGE,"E11.1"),sQuery(id+"F2.wireOp",EDGE,"E11.2")])]});
            var Q12;
            Q12=makeQuery(id+"F5.opExtrude","CAP_EDGE",EDGE,{"disambiguationData":[OSD([sQuery(id+"F2.wireOp",EDGE,"E11.2")])],"isStart":false});
            var Q13;
            Q13=makeQuery(id+"F4.opExtrude","CAP_EDGE",EDGE,{"disambiguationData":[OSD([sQuery(id+"F2.wireOp",EDGE,"E8.0")])],"isStart":false});
            var Q14;
            Q14=makeQuery(id+"F3.opExtrude","CAP_EDGE",EDGE,{"disambiguationData":[OSD([sQuery(id+"F2.wireOp",EDGE,"E7.0")])],"isStart":false});
            var Q15;
            Q15=makeQuery(id+"F3.opExtrude","SWEPT_EDGE",EDGE,{"disambiguationData":[OSD([sQuery(id+"F2.wireOp",EDGE,"E6.0"),sQuery(id+"F2.wireOp",EDGE,"E7.0")])]});
            chamfer(context, id + "F9", {"entities" : qUnion([Q0, Q1, Q2, Q3, Q4, Q5, Q6, Q7, Q8, Q9, Q10, Q11, Q12, Q13, Q14, Q15]), "width" : 1 * mm, "tangentPropagation" : true});
        }
    });
